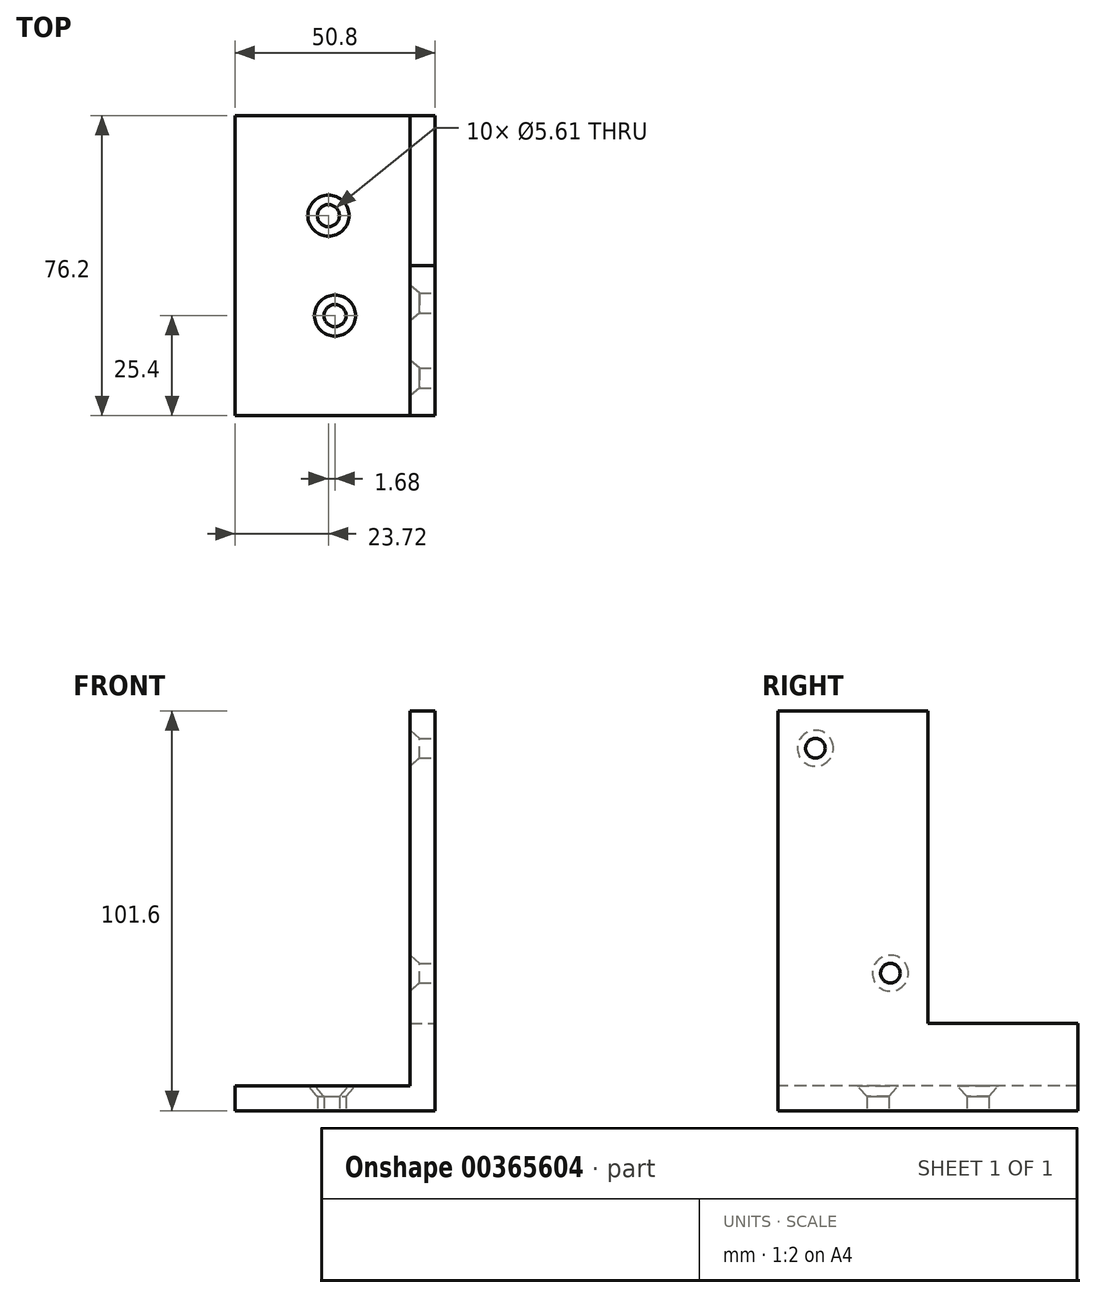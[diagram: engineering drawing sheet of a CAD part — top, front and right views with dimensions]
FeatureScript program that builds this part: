
annotation { "Feature Type Name" : "Feature", "Feature Type Description" : "" }
export const myFeature = defineFeature(function(context is Context, id is Id, definition is map)
    precondition{}
    {
        {
            var Q0;
            Q0=qCreatedBy(makeId("Front.planeOp"),FACE);
            var sketch = newSketch(context, id + "F0", { "sketchPlane" : qUnion([Q0])});
            skLineSegment(sketch, "E0", {"start": v(0, 0) * mm, "end": v(0, 101.6) * mm});
            skLineSegment(sketch, "E1", {"start": v(0, 101.6) * mm, "end": v(-6.35, 101.6) * mm});
            skLineSegment(sketch, "E2", {"start": v(-6.35, 101.6) * mm, "end": v(-6.35, 6.35) * mm});
            skLineSegment(sketch, "E3", {"start": v(-6.35, 6.35) * mm, "end": v(-50.8, 6.35) * mm});
            skLineSegment(sketch, "E4", {"start": v(-50.8, 6.35) * mm, "end": v(-50.8, 0) * mm});
            skLineSegment(sketch, "E5", {"start": v(-50.8, 0) * mm, "end": v(0, 0) * mm});
            skSolve(sketch);
        }
        {
            var Q0;
            Q0 = qSketchRegion(id + "F0", true);
            extrude(context, id + "F1", {"entities" : qUnion([Q0]), "oppositeDirection" : true, "depth" : 76.2 * mm, "offsetDistance" : 25.4 * mm});
        }
        {
            var Q0;
            Q0=makeQuery(id+"F1.opExtrude","SWEPT_FACE",FACE,{"disambiguationData":[OSD([sQuery(id+"F0.wireOp",EDGE,"E2")])]});
            var sketch = newSketch(context, id + "F2", { "sketchPlane" : qUnion([Q0])});
            skPoint(sketch, "E6", {"position": v(-9.52, 92.07) * mm});
            skPoint(sketch, "E7", {"position": v(-28.58, 34.92) * mm});
            skSolve(sketch);
        }
        {
            var Q0;
            Q0=sQuery(id+"F2.wireOp",VERTEX,"E6");
            var Q1;
            Q1=sQuery(id+"F2.wireOp",VERTEX,"E7");
            var Q2;
            Q2=makeQuery(id+"F1.opExtrude","SWEPT_BODY",BODY,{"disambiguationData":[OSD([sQuery(id+"F0.wireOp",EDGE,"E0"),sQuery(id+"F0.wireOp",EDGE,"E1"),sQuery(id+"F0.wireOp",EDGE,"E2"),sQuery(id+"F0.wireOp",EDGE,"E3"),sQuery(id+"F0.wireOp",EDGE,"E4"),sQuery(id+"F0.wireOp",EDGE,"E5")])]});
            hole(context, id + "F3", {"style" : HoleStyle.C_SINK, "endStyle" : HoleEndStyle.THROUGH, "standardTappedOrClearance" : lookupTablePath({ "fit" : "Normal (ASME)", "standard" : "ANSI", "size" : "#8", "type" : "Clearance" }), "standardBlindInLast" : lookupTablePath({ "fit" : "Normal", "standard" : "ANSI", "engagement" : "75%", "pitch" : "32 tpi", "size" : "#8", "type" : "Clearance & tapped" }), "holeDiameter" : 4.98 * mm, "cSinkDiameter" : 9.12 * mm, "cSinkAngle" : 82 * degree, "majorDiameter" : 6.35 * mm, "isTappedThrough" : true, "tappedDepth" : 12.7 * mm, "tapClearance" : 3, "locations" : qUnion([Q0, Q1]), "scope" : qUnion([Q2]), "startStyle" : HoleStartStyle.SKETCH});
        }
        {
            var Q0;
            Q0=makeQuery(id+"F1.opExtrude","SWEPT_FACE",FACE,{"disambiguationData":[OSD([sQuery(id+"F0.wireOp",EDGE,"E3")])]});
            var sketch = newSketch(context, id + "F4", { "sketchPlane" : qUnion([Q0])});
            skPoint(sketch, "E8", {"position": v(-27.08, 50.8) * mm});
            skPoint(sketch, "E9", {"position": v(-25.4, 25.4) * mm});
            skSolve(sketch);
        }
        {
            var Q0;
            Q0=sQuery(id+"F4.wireOp",VERTEX,"E9");
            var Q1;
            Q1=sQuery(id+"F4.wireOp",VERTEX,"E8");
            var Q2;
            Q2=makeQuery(id+"F1.opExtrude","SWEPT_BODY",BODY,{"disambiguationData":[OSD([sQuery(id+"F0.wireOp",EDGE,"E0"),sQuery(id+"F0.wireOp",EDGE,"E1"),sQuery(id+"F0.wireOp",EDGE,"E2"),sQuery(id+"F0.wireOp",EDGE,"E3"),sQuery(id+"F0.wireOp",EDGE,"E4"),sQuery(id+"F0.wireOp",EDGE,"E5")])]});
            hole(context, id + "F5", {"style" : HoleStyle.C_SINK, "endStyle" : HoleEndStyle.THROUGH, "standardTappedOrClearance" : lookupTablePath({ "fit" : "Normal (ASME)", "standard" : "ANSI", "size" : "#10", "type" : "Clearance" }), "standardBlindInLast" : lookupTablePath({ "fit" : "Normal", "standard" : "ANSI", "engagement" : "75%", "pitch" : "24 tpi", "size" : "#10", "type" : "Clearance & tapped" }), "holeDiameter" : 5.61 * mm, "cSinkDiameter" : 10.44 * mm, "cSinkAngle" : 82 * degree, "majorDiameter" : 6.35 * mm, "isTappedThrough" : true, "tappedDepth" : 12.7 * mm, "tapClearance" : 3, "locations" : qUnion([Q0, Q1]), "scope" : qUnion([Q2]), "startStyle" : HoleStartStyle.SKETCH});
        }
        {
            var Q0;
            Q0=makeQuery(id+"F1.opExtrude","SWEPT_FACE",FACE,{"disambiguationData":[OSD([sQuery(id+"F0.wireOp",EDGE,"E0")])]});
            var sketch = newSketch(context, id + "F6", { "sketchPlane" : qUnion([Q0])});
            skLineSegment(sketch, "E10.bottom", {"start": v(76.2, 101.6) * mm, "end": v(38.1, 101.6) * mm});
            skLineSegment(sketch, "E10.top", {"start": v(76.2, 22.22) * mm, "end": v(38.1, 22.22) * mm});
            skLineSegment(sketch, "E10.left", {"start": v(76.2, 101.6) * mm, "end": v(76.2, 22.23) * mm});
            skLineSegment(sketch, "E10.right", {"start": v(38.1, 101.6) * mm, "end": v(38.1, 22.23) * mm});
            skSolve(sketch);
        }
        {
            var Q0;
            Q0 = qSketchRegion(id + "F6", true);
            extrude(context, id + "F7", {"entities" : qUnion([Q0]), "operationType" : NewBodyOperationType.REMOVE, "endBound" : BoundingType.THROUGH_ALL, "oppositeDirection" : true, "depth" : 25.4 * mm, "offsetDistance" : 25.4 * mm});
        }
    });
